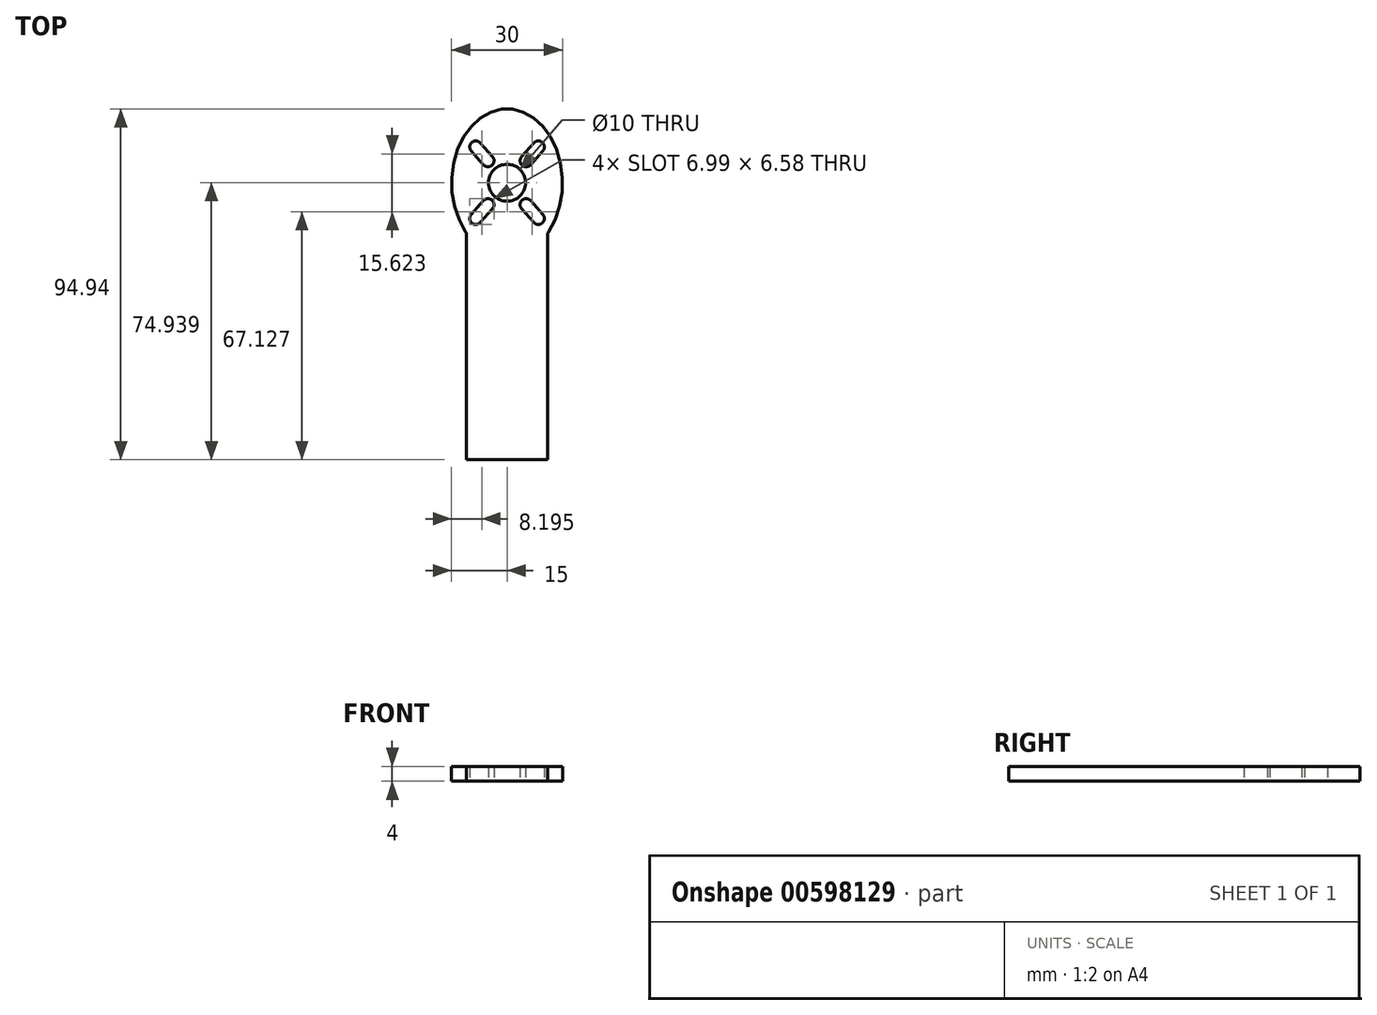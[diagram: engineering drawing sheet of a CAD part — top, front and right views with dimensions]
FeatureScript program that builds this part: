
annotation { "Feature Type Name" : "Feature", "Feature Type Description" : "" }
export const myFeature = defineFeature(function(context is Context, id is Id, definition is map)
    precondition{}
    {
        {
            var Q0;
            Q0=qCreatedBy(makeId("Top.planeOp"),FACE);
            var sketch = newSketch(context, id + "F0", { "sketchPlane" : qUnion([Q0])});
            skLineSegment(sketch, "E0.top", {"start": v(11, -30.72) * mm, "end": v(-11, -30.72) * mm});
            skLineSegment(sketch, "E0.left", {"start": v(11, 30.25) * mm, "end": v(11, -30.72) * mm});
            skLineSegment(sketch, "E0.right", {"start": v(-11, 30.25) * mm, "end": v(-11, -30.72) * mm});
            skPoint(sketch, "E0.middle", {"position": v(0, 0) * mm});
            skEllipticalArc(sketch, "E1", {});
            skCircle(sketch, "E2", {"center": v(0, 44.22) * mm, "radius": 5 * mm});
            skArc(sketch, "E3", {"start": v(7.25, 33.46) * mm, "mid": v(9.55, 33.32) * mm, "end": v(9.68, 35.62) * mm});
            skArc(sketch, "E4", {"start": v(6.36, 39.36) * mm, "mid": v(4.06, 39.5) * mm, "end": v(3.93, 37.2) * mm});
            skLineSegment(sketch, "E5", {"start": v(6.36, 39.36) * mm, "end": v(9.68, 35.62) * mm});
            skLineSegment(sketch, "E6", {"start": v(3.93, 37.2) * mm, "end": v(7.25, 33.46) * mm});
            skArc(sketch, "E7", {"start": v(9.68, 52.82) * mm, "mid": v(9.55, 55.12) * mm, "end": v(7.25, 54.98) * mm});
            skArc(sketch, "E8", {"start": v(3.93, 51.25) * mm, "mid": v(4.06, 48.94) * mm, "end": v(6.36, 49.08) * mm});
            skLineSegment(sketch, "E9", {"start": v(3.93, 51.25) * mm, "end": v(7.25, 54.98) * mm});
            skLineSegment(sketch, "E10", {"start": v(6.36, 49.08) * mm, "end": v(9.68, 52.82) * mm});
            skArc(sketch, "E11", {"start": v(-6.36, 49.08) * mm, "mid": v(-4.06, 48.94) * mm, "end": v(-3.93, 51.25) * mm});
            skArc(sketch, "E12", {"start": v(-7.25, 54.98) * mm, "mid": v(-9.55, 55.12) * mm, "end": v(-9.68, 52.82) * mm});
            skLineSegment(sketch, "E13", {"start": v(-7.25, 54.98) * mm, "end": v(-3.93, 51.25) * mm});
            skLineSegment(sketch, "E14", {"start": v(-9.68, 52.82) * mm, "end": v(-6.36, 49.08) * mm});
            skArc(sketch, "E15", {"start": v(-3.93, 37.2) * mm, "mid": v(-4.06, 39.5) * mm, "end": v(-6.36, 39.36) * mm});
            skArc(sketch, "E16", {"start": v(-9.68, 35.62) * mm, "mid": v(-9.55, 33.32) * mm, "end": v(-7.25, 33.46) * mm});
            skLineSegment(sketch, "E17", {"start": v(-9.68, 35.62) * mm, "end": v(-6.36, 39.36) * mm});
            skLineSegment(sketch, "E18", {"start": v(-7.25, 33.46) * mm, "end": v(-3.93, 37.2) * mm});
            skCircle(sketch, "E19", {"center": v(0, 44.22) * mm, "radius": 7.86 * mm});
            skCircle(sketch, "E20", {"center": v(0, 44.22) * mm, "radius": 12.86 * mm});
            skPoint(sketch, "E21", {"position": v(-12.86, 44.22) * mm});
            skPoint(sketch, "E22", {"position": v(-7.86, 44.22) * mm});
            skPoint(sketch, "E23", {"position": v(-5, 44.22) * mm});
            skPoint(sketch, "E24", {"position": v(5, 44.22) * mm});
            skPoint(sketch, "E25", {"position": v(7.86, 44.22) * mm});
            skPoint(sketch, "E26", {"position": v(12.86, 44.22) * mm});
            skPoint(sketch, "E27", {"position": v(0, 30.72) * mm});
            skArc(sketch, "E28.filletArc", {"start": v(11.2, 30.92) * mm, "mid": v(11.05, 30.6) * mm, "end": v(11, 30.25) * mm});
            skArc(sketch, "E29.filletArc", {"start": v(-11, 30.25) * mm, "mid": v(-11.05, 30.6) * mm, "end": v(-11.2, 30.92) * mm});
            skPoint(sketch, "E0.bottom.start.orphan", {"position": v(11, 30.72) * mm});
            const initialGuessF0  = {"E1": [0, 0.04421883507072926, 0, -1, 0.02, 0.015, 0.8435244991571995, 5.439660808022385]};
            skSetInitialGuess(sketch, initialGuessF0);
            skSolve(sketch);
        }
        {
            var Q0;
            Q0=makeQuery(id+"F0.imprint","IMPRINT",FACE,{"disambiguationData":[TD([[makeQuery(id+"F0.imprint","IMPRINT",EDGE,{"derivedFrom":sQuery(id+"F0.wireOp",EDGE,"E0.top")}),-1.0]])]});
            var Q1;
            {var subQ7=sQuery(id+"F0.wireOp",EDGE,"E6");var subQ8=sQuery(id+"F0.wireOp",EDGE,"E4");var subQ9=makeQuery(id+"F0.imprint","INTERSECT",VERTEX,{"derivedFrom":[subQ8,subQ7]});Q1=makeQuery(id+"F0.imprint","IMPRINT",FACE,{"disambiguationData":[TD([[makeQuery(id+"F0.imprint","IMPRINT",EDGE,{"disambiguationData":[TD([[subQ9,1.0]])],"derivedFrom":subQ8}),-1.0]])]});}
            var Q2;
            {var subQ5=sQuery(id+"F0.wireOp",EDGE,"E5");var subQ7=sQuery(id+"F0.wireOp",EDGE,"E4");var subQ8=makeQuery(id+"F0.imprint","INTERSECT",VERTEX,{"derivedFrom":[subQ7,subQ5]});Q2=makeQuery(id+"F0.imprint","IMPRINT",FACE,{"disambiguationData":[TD([[makeQuery(id+"F0.imprint","IMPRINT",EDGE,{"disambiguationData":[TD([[subQ8,-1.0]])],"derivedFrom":subQ7}),-1.0]])]});}
            var Q3;
            {var subQ5=sQuery(id+"F0.wireOp",EDGE,"E14");var subQ6=sQuery(id+"F0.wireOp",EDGE,"E11");var subQ7=makeQuery(id+"F0.imprint","INTERSECT",VERTEX,{"derivedFrom":[subQ6,subQ5]});Q3=makeQuery(id+"F0.imprint","IMPRINT",FACE,{"disambiguationData":[TD([[makeQuery(id+"F0.imprint","IMPRINT",EDGE,{"disambiguationData":[TD([[subQ7,-1.0]])],"derivedFrom":subQ6}),-1.0]])]});}
            var Q4;
            {var subQ7=sQuery(id+"F0.wireOp",EDGE,"E9");var subQ8=sQuery(id+"F0.wireOp",EDGE,"E8");var subQ9=makeQuery(id+"F0.imprint","INTERSECT",VERTEX,{"derivedFrom":[subQ8,subQ7]});Q4=makeQuery(id+"F0.imprint","IMPRINT",FACE,{"disambiguationData":[TD([[makeQuery(id+"F0.imprint","IMPRINT",EDGE,{"disambiguationData":[TD([[subQ9,-1.0]])],"derivedFrom":subQ8}),-1.0]])]});}
            var Q5;
            Q5=makeQuery(id+"F0.imprint","IMPRINT",FACE,{"disambiguationData":[TD([[makeQuery(id+"F0.imprint","IMPRINT",EDGE,{"derivedFrom":sQuery(id+"F0.wireOp",EDGE,"E2")}),-1.0]])]});
            extrude(context, id + "F1", {"entities" : qUnion([Q0, Q1, Q2, Q3, Q4, Q5]), "depth" : 4 * mm, "offsetDistance" : 25 * mm});
        }
    });
